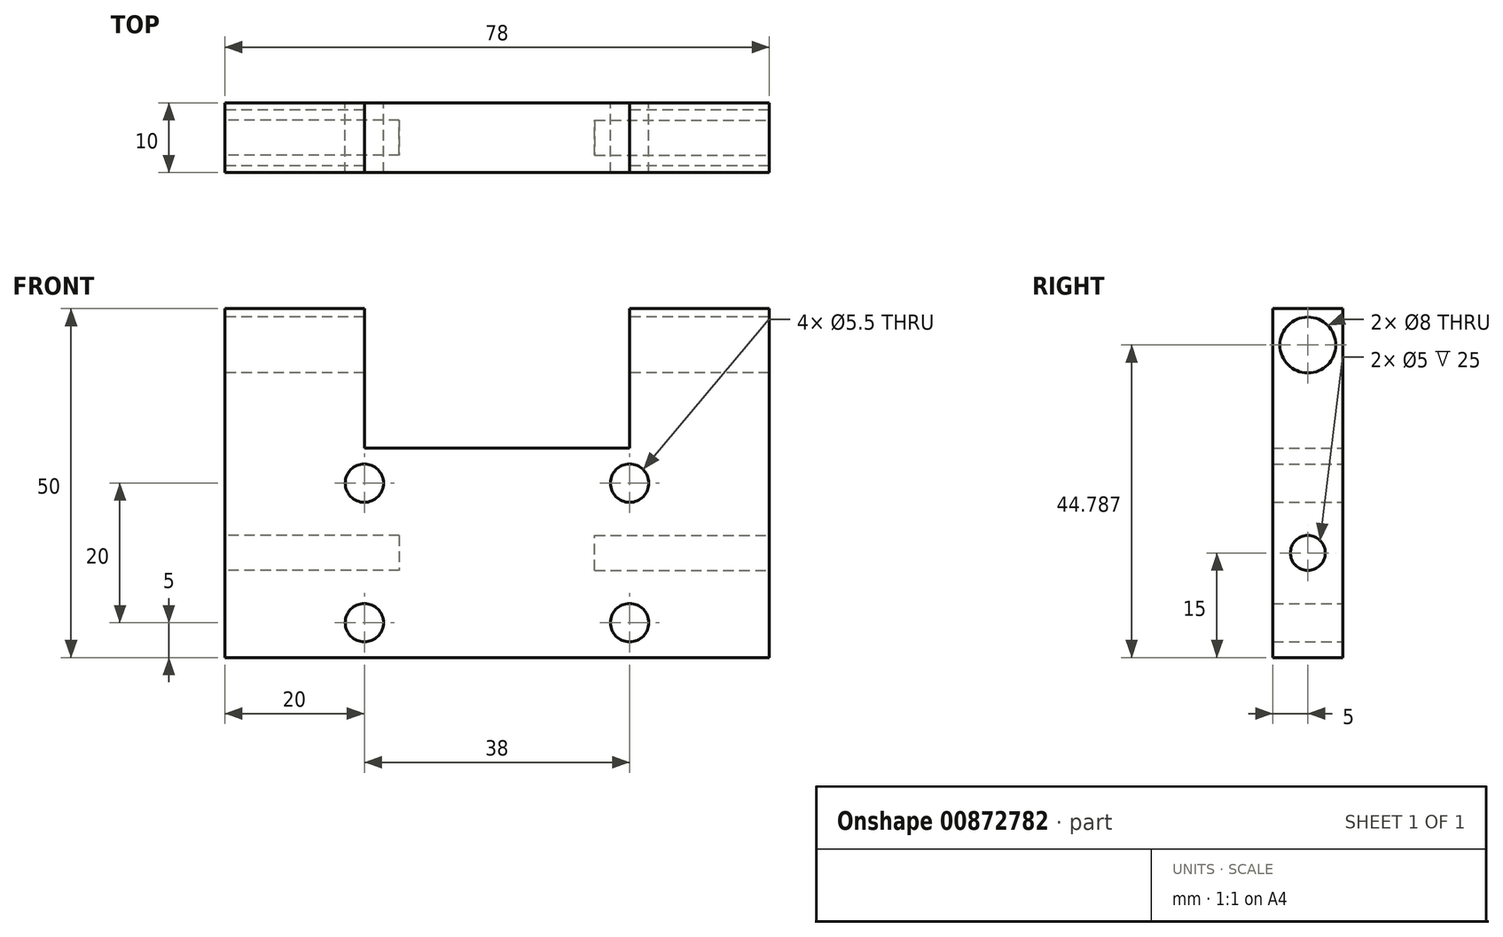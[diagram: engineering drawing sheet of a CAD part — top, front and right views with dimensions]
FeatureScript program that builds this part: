
annotation { "Feature Type Name" : "Feature", "Feature Type Description" : "" }
export const myFeature = defineFeature(function(context is Context, id is Id, definition is map)
    precondition{}
    {
        {
            var Q0;
            Q0=qCreatedBy(makeId("Front.planeOp"),FACE);
            var sketch = newSketch(context, id + "F0", { "sketchPlane" : qUnion([Q0])});
            skLineSegment(sketch, "E0.bottom", {"start": v(-39, 24) * mm, "end": v(-19, 24) * mm});
            skPoint(sketch, "E0.middle", {"position": v(0, 0) * mm});
            skPoint(sketch, "E1.start.orphan", {"position": v(-19, 24) * mm});
            skLineSegment(sketch, "E2.trimOffspring", {"start": v(19, 24) * mm, "end": v(39, 24) * mm});
            skPoint(sketch, "E3.top.start.orphan", {"position": v(-19, 4) * mm});
            skLineSegment(sketch, "E4.top", {"start": v(19, 4) * mm, "end": v(-19, 4) * mm});
            skLineSegment(sketch, "E4.left", {"start": v(19, 24) * mm, "end": v(19, 4) * mm});
            skLineSegment(sketch, "E4.right", {"start": v(-19, 24) * mm, "end": v(-19, 4) * mm});
            skCircle(sketch, "E5", {"center": v(-19, -1) * mm, "radius": 2.75 * mm});
            skCircle(sketch, "E6", {"center": v(19, -1) * mm, "radius": 2.75 * mm});
            skLineSegment(sketch, "E7.top", {"start": v(-39, -26) * mm, "end": v(39, -26) * mm});
            skLineSegment(sketch, "E8", {"start": v(-39, 24) * mm, "end": v(-39, -26) * mm});
            skLineSegment(sketch, "E9", {"start": v(39, 24) * mm, "end": v(39, -26) * mm});
            skCircle(sketch, "E10", {"center": v(-19, -21) * mm, "radius": 2.75 * mm});
            skCircle(sketch, "E11", {"center": v(19, -21) * mm, "radius": 2.75 * mm});
            skSolve(sketch);
        }
        {
            var Q0;
            Q0=makeQuery(id+"F0.imprint","IMPRINT",FACE,{"disambiguationData":[TD([[makeQuery(id+"F0.imprint","IMPRINT",EDGE,{"derivedFrom":sQuery(id+"F0.wireOp",EDGE,"E0.bottom")}),-1.0]])]});
            extrude(context, id + "F1", {"entities" : qUnion([Q0]), "depth" : 10 * mm, "offsetDistance" : 25 * mm});
        }
        {
            var Q0;
            Q0=makeQuery(id+"F1.opExtrude","SWEPT_FACE",FACE,{"disambiguationData":[OSD([sQuery(id+"F0.wireOp",EDGE,"E8")])]});
            var sketch = newSketch(context, id + "F2", { "sketchPlane" : qUnion([Q0])});
            skCircle(sketch, "E12", {"center": v(5, 18.79) * mm, "radius": 4 * mm});
            skPoint(sketch, "E12.centerSnap0", {"position": v(5, 24) * mm});
            skSolve(sketch);
        }
        {
            var Q0;
            Q0=qSketchRegion(id+"F2",true);
            extrude(context, id + "F3", {"entities" : qUnion([Q0]), "operationType" : NewBodyOperationType.REMOVE, "oppositeDirection" : true, "depth" : 99 * mm, "offsetDistance" : 25 * mm});
        }
        {
            var Q0;
            Q0=makeQuery(id+"F1.opExtrude","SWEPT_FACE",FACE,{"disambiguationData":[OSD([sQuery(id+"F0.wireOp",EDGE,"E8")])]});
            var sketch = newSketch(context, id + "F4", { "sketchPlane" : qUnion([Q0])});
            skCircle(sketch, "E13", {"center": v(5, -11) * mm, "radius": 2.5 * mm});
            skPoint(sketch, "E13.centerSnap0", {"position": v(5, -26) * mm});
            skSolve(sketch);
        }
        {
            var Q0;
            Q0=qSketchRegion(id+"F4",true);
            extrude(context, id + "F5", {"entities" : qUnion([Q0]), "operationType" : NewBodyOperationType.REMOVE, "oppositeDirection" : true, "depth" : 25 * mm, "offsetDistance" : 25 * mm});
        }
        {
            var Q0;
            Q0=makeQuery(id+"F1.opExtrude","SWEPT_FACE",FACE,{"disambiguationData":[OSD([sQuery(id+"F0.wireOp",EDGE,"E9")])]});
            var sketch = newSketch(context, id + "F6", { "sketchPlane" : qUnion([Q0])});
            skCircle(sketch, "E14", {"center": v(-5, -11) * mm, "radius": 2.5 * mm});
            skPoint(sketch, "E14.centerSnap0", {"position": v(-5, -26) * mm});
            skSolve(sketch);
        }
        {
            var Q0;
            Q0=qSketchRegion(id+"F6",true);
            extrude(context, id + "F7", {"entities" : qUnion([Q0]), "operationType" : NewBodyOperationType.REMOVE, "oppositeDirection" : true, "depth" : 25 * mm, "offsetDistance" : 25 * mm});
        }
    });
